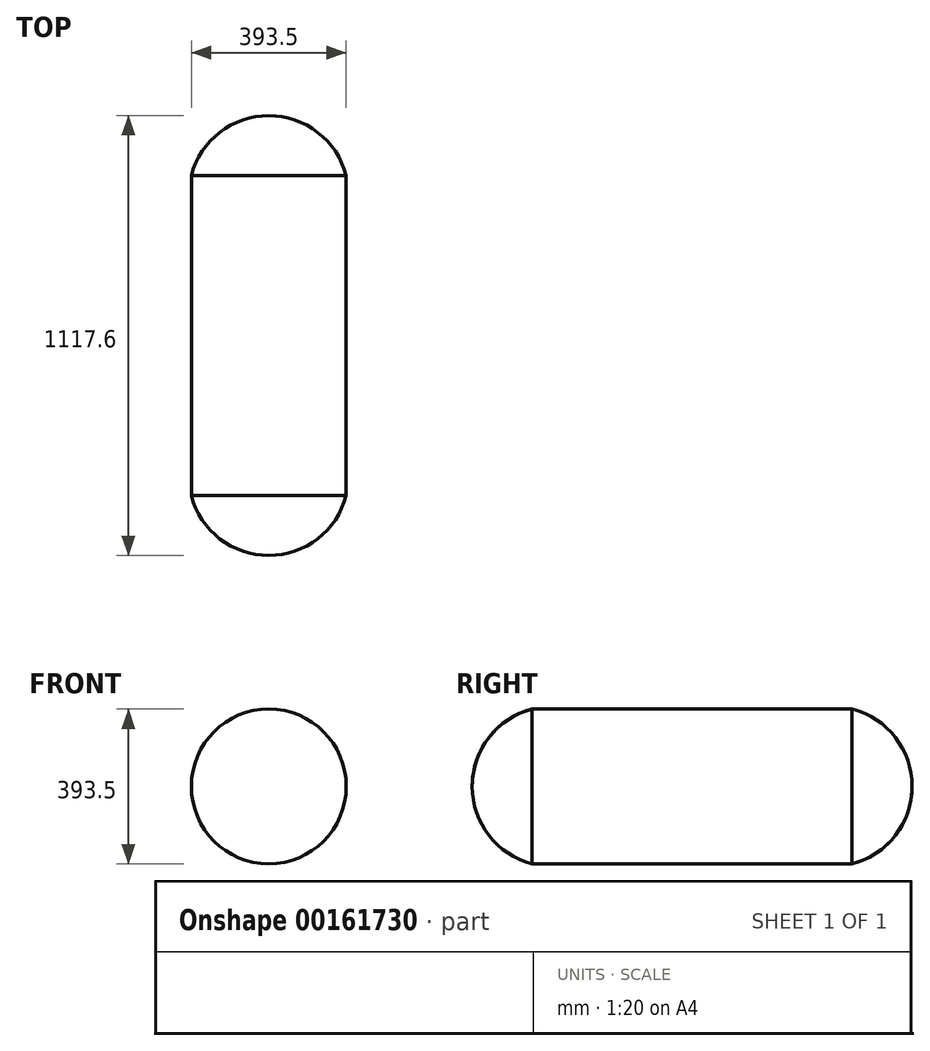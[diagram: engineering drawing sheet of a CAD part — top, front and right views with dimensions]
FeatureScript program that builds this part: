
annotation { "Feature Type Name" : "Feature", "Feature Type Description" : "" }
export const myFeature = defineFeature(function(context is Context, id is Id, definition is map)
    precondition{}
    {
        {
            var Q0;
            Q0=qCreatedBy(makeId("Right.planeOp"),FACE);
            var sketch = newSketch(context, id + "F0", { "sketchPlane" : qUnion([Q0])});
            skLineSegment(sketch, "E0", {"start": v(-406.4, 0) * mm, "end": v(406.4, 0) * mm});
            skArc(sketch, "E1", {"start": v(-558.8, 196.75) * mm, "mid": v(-516.24, 72.31) * mm, "end": v(-406.4, 0) * mm});
            skArc(sketch, "E2", {"start": v(406.4, 0) * mm, "mid": v(516.24, 72.31) * mm, "end": v(558.8, 196.75) * mm});
            skLineSegment(sketch, "E3", {"start": v(-558.8, 196.75) * mm, "end": v(558.8, 196.75) * mm});
            skSolve(sketch);
        }
        {
            var Q0;
            Q0 = qSketchRegion(id + "F0", true);
            var Q1;
            Q1=sQuery(id+"F0.wireOp",EDGE,"E3");
            revolve(context, id + "F1", {"entities" : qUnion([Q0]), "axis" : qUnion([Q1]), "revolveType" : RevolveType.FULL});
        }
    });
